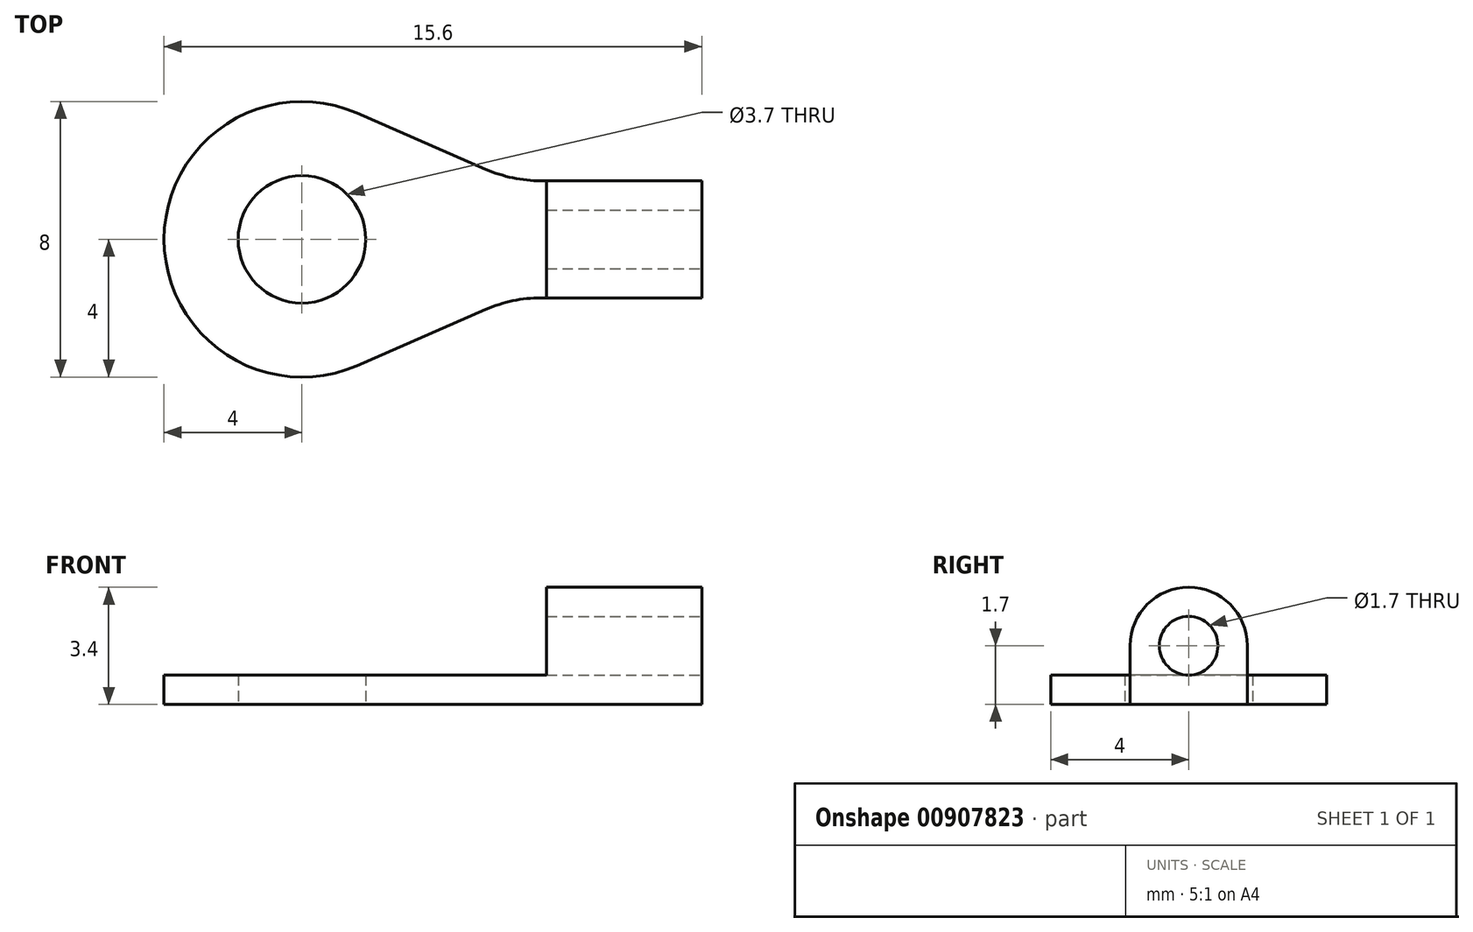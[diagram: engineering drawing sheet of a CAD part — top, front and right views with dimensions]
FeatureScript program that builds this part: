
annotation { "Feature Type Name" : "Feature", "Feature Type Description" : "" }
export const myFeature = defineFeature(function(context is Context, id is Id, definition is map)
    precondition{}
    {
        {
            var Q0;
            Q0=qCreatedBy(makeId("Top.planeOp"),FACE);
            var sketch = newSketch(context, id + "F0", { "sketchPlane" : qUnion([Q0])});
            skLineSegment(sketch, "E0.left", {"start": v(0, 4) * mm, "end": v(0, 4) * mm});
            skLineSegment(sketch, "E0.right", {"start": v(15.6, 2.3) * mm, "end": v(15.6, 5.7) * mm});
            skPoint(sketch, "E1.visualSharp", {"position": v(0, 8) * mm});
            skArc(sketch, "E1.filletArc", {"start": v(4, 8) * mm, "mid": v(1.17, 6.83) * mm, "end": v(0, 4) * mm});
            skPoint(sketch, "E2.visualSharp", {"position": v(0, 0) * mm});
            skArc(sketch, "E2.filletArc", {"start": v(0, 4) * mm, "mid": v(1.17, 1.17) * mm, "end": v(4, 0) * mm});
            skLineSegment(sketch, "E3.bottom", {"start": v(10.94, 2.3) * mm, "end": v(15.6, 2.3) * mm});
            skLineSegment(sketch, "E3.top", {"start": v(10.94, 5.7) * mm, "end": v(15.6, 5.7) * mm});
            skPoint(sketch, "E3.middle", {"position": v(15.6, 4) * mm});
            skArc(sketch, "E4", {"start": v(5.6, 7.67) * mm, "mid": v(0, 4) * mm, "end": v(5.6, 0.33) * mm});
            skCircle(sketch, "E5", {"center": v(4, 4) * mm, "radius": 1.85 * mm});
            skLineSegment(sketch, "E6", {"start": v(9.33, 6.03) * mm, "end": v(5.6, 7.67) * mm});
            skLineSegment(sketch, "E7", {"start": v(9.33, 1.97) * mm, "end": v(5.6, 0.33) * mm});
            skPoint(sketch, "E8.visualSharp", {"position": v(10.1, 5.7) * mm});
            skArc(sketch, "E8.filletArc", {"start": v(9.33, 6.03) * mm, "mid": v(10.12, 5.78) * mm, "end": v(10.94, 5.7) * mm});
            skPoint(sketch, "E9.visualSharp", {"position": v(10.1, 2.3) * mm});
            skArc(sketch, "E9.filletArc", {"start": v(10.94, 2.3) * mm, "mid": v(10.12, 2.22) * mm, "end": v(9.33, 1.97) * mm});
            skPoint(sketch, "E10.orphan", {"position": v(20.1, 5.7) * mm});
            skPoint(sketch, "E11.orphan", {"position": v(20.1, 2.3) * mm});
            skPoint(sketch, "E0.bottom.end.orphan", {"position": v(15.6, 0) * mm});
            skPoint(sketch, "E0.top.end.orphan", {"position": v(15.6, 8) * mm});
            skPoint(sketch, "E3.left.end.orphan", {"position": v(11.1, 5.7) * mm});
            skPoint(sketch, "E3.left.start.orphan", {"position": v(11.1, 2.3) * mm});
            skSolve(sketch);
        }
        {
            var Q0;
            Q0 = qSketchRegion(id + "F0", true);
            extrude(context, id + "F1", {"entities" : qUnion([Q0]), "depth" : 0.85 * mm, "offsetDistance" : 25 * mm});
        }
        {
            var Q0;
            Q0=makeQuery(id+"F1.opExtrude","CAP_FACE",FACE,{"disambiguationData":[OSD([sQuery(id+"F0.wireOp",EDGE,"E0.right"),sQuery(id+"F0.wireOp",EDGE,"E3.bottom"),sQuery(id+"F0.wireOp",EDGE,"E3.top"),sQuery(id+"F0.wireOp",EDGE,"E4"),sQuery(id+"F0.wireOp",EDGE,"E5"),sQuery(id+"F0.wireOp",EDGE,"E6"),sQuery(id+"F0.wireOp",EDGE,"E7"),sQuery(id+"F0.wireOp",EDGE,"E8.filletArc"),sQuery(id+"F0.wireOp",EDGE,"E9.filletArc")])],"isStart":false});
            var sketch = newSketch(context, id + "F2", { "sketchPlane" : qUnion([Q0])});
            skLineSegment(sketch, "E12.bottom", {"start": v(15.6, 5.7) * mm, "end": v(11.1, 5.7) * mm});
            skLineSegment(sketch, "E12.top", {"start": v(15.6, 2.3) * mm, "end": v(11.1, 2.3) * mm});
            skLineSegment(sketch, "E12.left", {"start": v(15.6, 5.7) * mm, "end": v(15.6, 2.3) * mm});
            skLineSegment(sketch, "E12.right", {"start": v(11.1, 5.7) * mm, "end": v(11.1, 2.3) * mm});
            skSolve(sketch);
        }
        {
            var Q0;
            Q0 = qSketchRegion(id + "F2", true);
            var Q1;
            Q1=makeQuery(id+"F2.imprint","IMPRINT",FACE,{"disambiguationData":[TD([[makeQuery(id+"F2.imprint","IMPRINT",EDGE,{"derivedFrom":sQuery(id+"F2.wireOp",EDGE,"E12.bottom")}),-1.0]])]});
            extrude(context, id + "F3", {"entities" : qUnion([Q0, Q1]), "operationType" : NewBodyOperationType.ADD, "depth" : 2.55 * mm, "offsetDistance" : 25 * mm});
        }
        {
            var Q0;
            Q0=makeQuery(id+"F3.opExtrude","CAP_EDGE",EDGE,{"disambiguationData":[OSD([sQuery(id+"F2.wireOp",EDGE,"E12.bottom")])],"isStart":false});
            var Q1;
            Q1=makeQuery(id+"F3.opExtrude","CAP_EDGE",EDGE,{"disambiguationData":[OSD([sQuery(id+"F2.wireOp",EDGE,"E12.top")])],"isStart":false});
            fillet(context, id + "F4", {"entities" : qUnion([Q0, Q1]), "radius" : 1.7 * mm, "tangentPropagation" : true, "allowEdgeOverflow" : false});
        }
        {
            var Q0;
            Q0=makeQuery(id+"F3.boolean.opBoolean","MERGE",FACE,{"derivedFrom":[makeQuery(id+"F1.opExtrude","SWEPT_FACE",FACE,{"disambiguationData":[OSD([sQuery(id+"F0.wireOp",EDGE,"E0.right")])]}),makeQuery(id+"F3.opExtrude","SWEPT_FACE",FACE,{"disambiguationData":[OSD([sQuery(id+"F2.wireOp",EDGE,"E12.left")])]})]});
            var sketch = newSketch(context, id + "F5", { "sketchPlane" : qUnion([Q0])});
            skCircle(sketch, "E13", {"center": v(4, 1.7) * mm, "radius": 0.85 * mm});
            skSolve(sketch);
        }
        {
            var Q0;
            Q0=makeQuery(id+"F5.imprint","IMPRINT",FACE,{"disambiguationData":[TD([[makeQuery(id+"F5.imprint","IMPRINT",EDGE,{"derivedFrom":sQuery(id+"F5.wireOp",EDGE,"E13")}),1.0]])]});
            extrude(context, id + "F6", {"entities" : qUnion([Q0]), "operationType" : NewBodyOperationType.REMOVE, "oppositeDirection" : true, "depth" : 25 * mm, "offsetDistance" : 25 * mm});
        }
    });
